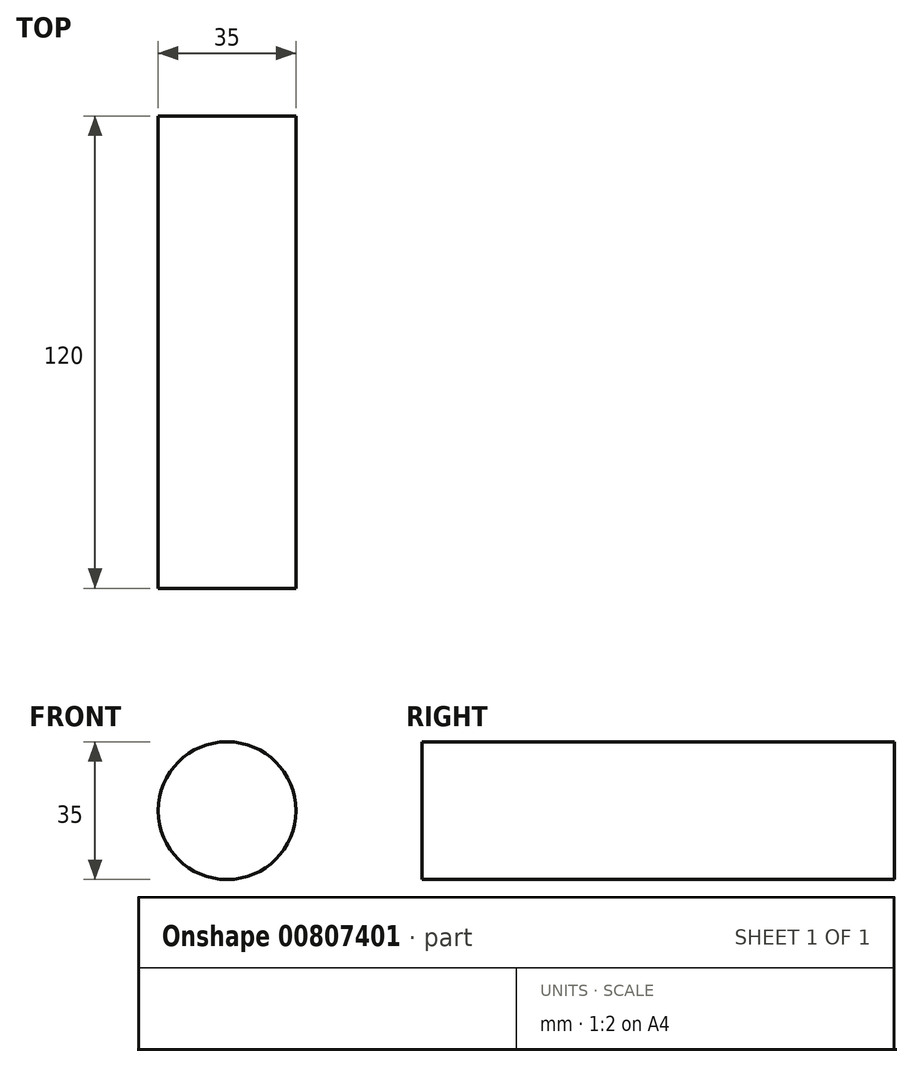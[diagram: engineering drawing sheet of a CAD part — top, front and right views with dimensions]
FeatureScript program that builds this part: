
annotation { "Feature Type Name" : "Feature", "Feature Type Description" : "" }
export const myFeature = defineFeature(function(context is Context, id is Id, definition is map)
    precondition{}
    {
        {
            var Q0;
            Q0=qCreatedBy(makeId("Front.planeOp"),FACE);
            var sketch = newSketch(context, id + "F0", { "sketchPlane" : qUnion([Q0])});
            skCircle(sketch, "E0", {"center": v(0, 0) * mm, "radius": 17.5 * mm});
            skSolve(sketch);
        }
        {
            var Q0;
            Q0 = qSketchRegion(id + "F0", true);
            extrude(context, id + "F1", {"entities" : qUnion([Q0]), "depth" : 120 * mm, "offsetDistance" : 25 * mm});
        }
    });
